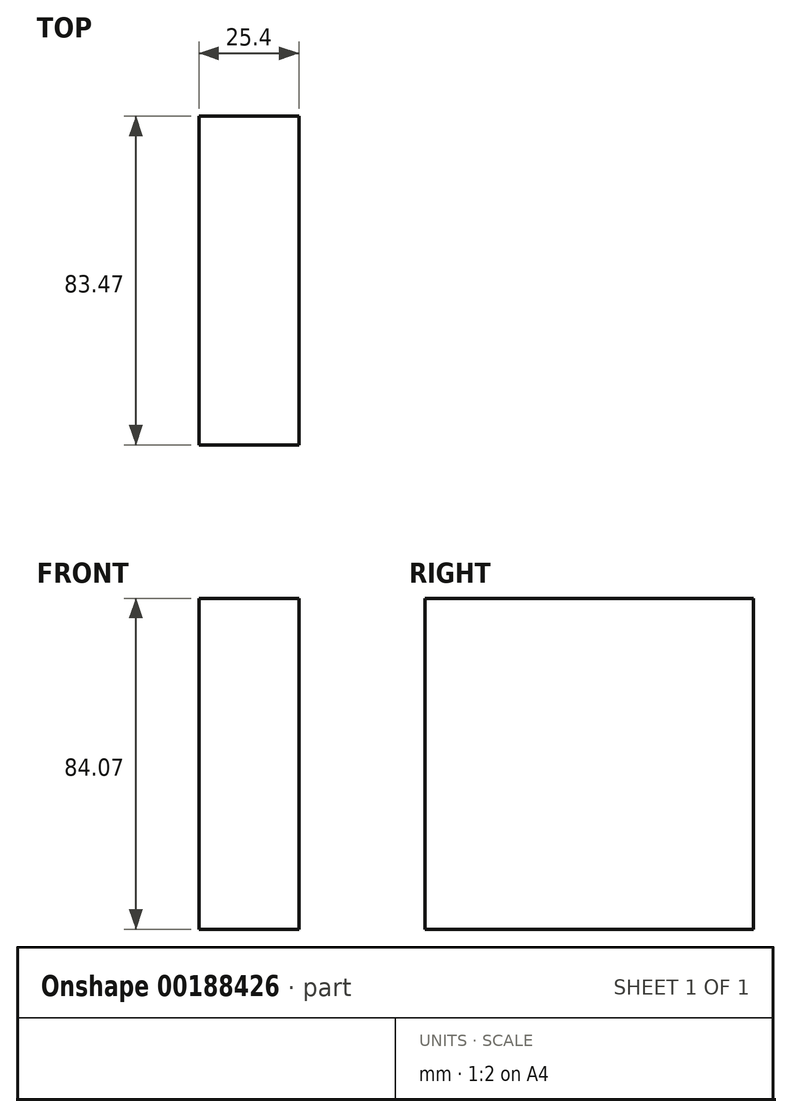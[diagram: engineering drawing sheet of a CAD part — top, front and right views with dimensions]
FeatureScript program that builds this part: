
annotation { "Feature Type Name" : "Feature", "Feature Type Description" : "" }
export const myFeature = defineFeature(function(context is Context, id is Id, definition is map)
    precondition{}
    {
        {
            var Q0;
            Q0=qCreatedBy(makeId("Right.planeOp"),FACE);
            var sketch = newSketch(context, id + "F0", { "sketchPlane" : qUnion([Q0])});
            skLineSegment(sketch, "E0.bottom", {"start": v(-8.16, 18.7) * mm, "end": v(75.31, 18.7) * mm});
            skLineSegment(sketch, "E0.top", {"start": v(-8.16, -65.37) * mm, "end": v(75.31, -65.37) * mm});
            skLineSegment(sketch, "E0.left", {"start": v(-8.16, 18.7) * mm, "end": v(-8.16, -65.37) * mm});
            skLineSegment(sketch, "E0.right", {"start": v(75.31, 18.7) * mm, "end": v(75.31, -65.37) * mm});
            skSolve(sketch);
        }
        {
            var Q0;
            Q0 = qSketchRegion(id + "F0", true);
            extrude(context, id + "F1", {"entities" : qUnion([Q0]), "depth" : 25.4 * mm});
        }
    });
